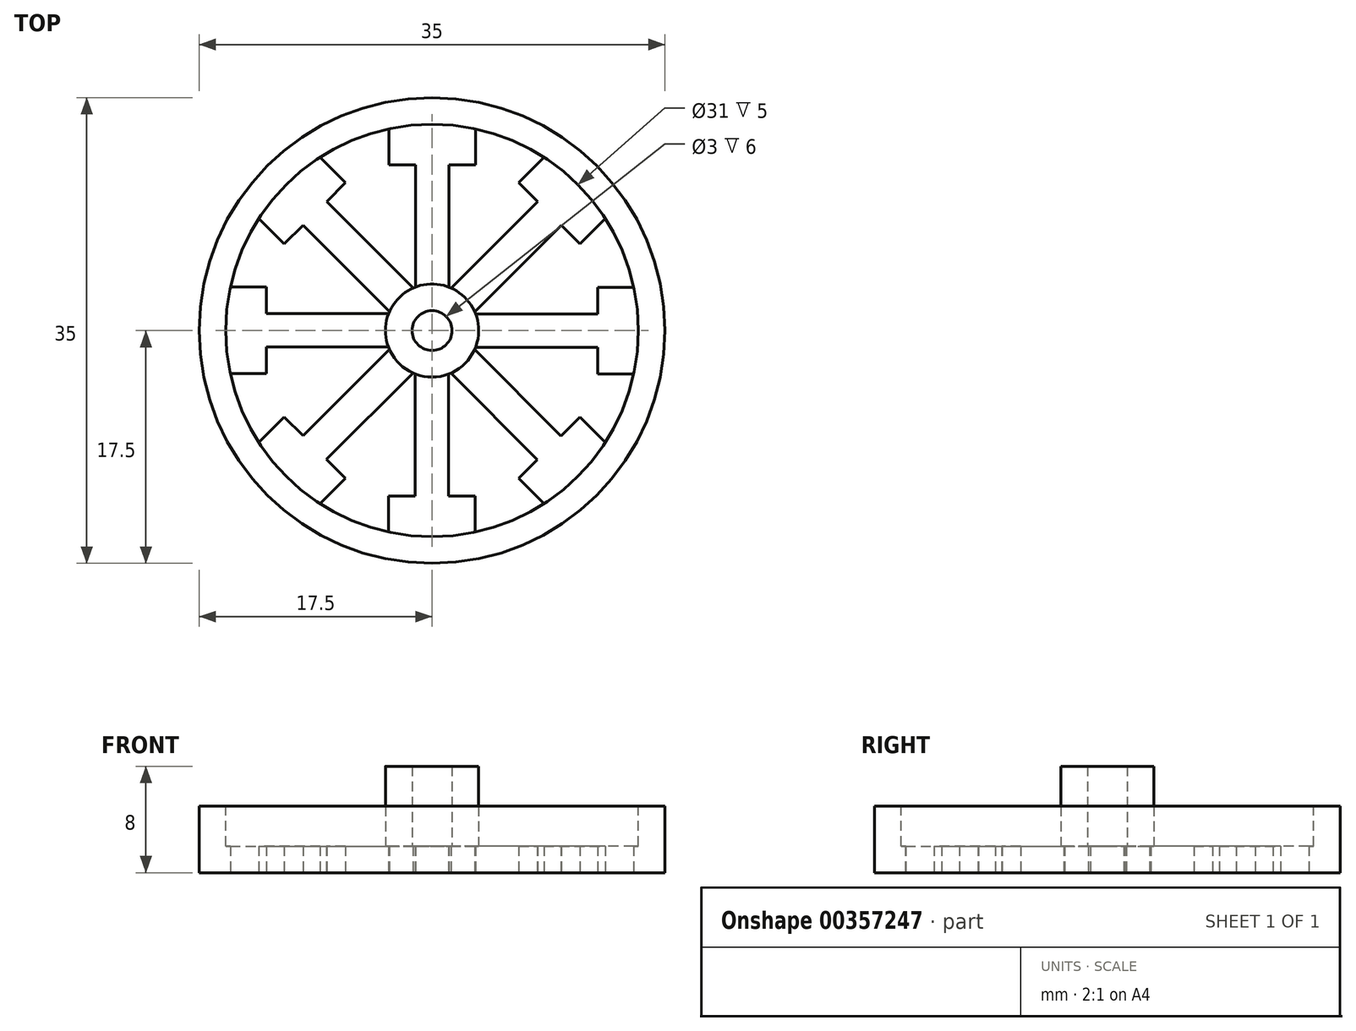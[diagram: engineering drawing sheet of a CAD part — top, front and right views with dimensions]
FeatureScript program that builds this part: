
annotation { "Feature Type Name" : "Feature", "Feature Type Description" : "" }
export const myFeature = defineFeature(function(context is Context, id is Id, definition is map)
    precondition{}
    {
        {
            var Q0;
            Q0=qCreatedBy(makeId("Top.planeOp"),FACE);
            var sketch = newSketch(context, id + "F0", { "sketchPlane" : qUnion([Q0])});
            skCircle(sketch, "E0", {"center": v(0, 0) * mm, "radius": 17.5 * mm});
            skSolve(sketch);
        }
        {
            var Q0;
            Q0=makeQuery(id+"F0.imprint","IMPRINT",FACE,{"disambiguationData":[TD([[makeQuery(id+"F0.imprint","IMPRINT",EDGE,{"derivedFrom":sQuery(id+"F0.wireOp",EDGE,"E0")}),1.0]])]});
            extrude(context, id + "F1", {"entities" : qUnion([Q0]), "depth" : 5 * mm});
        }
        {
            var Q0;
            Q0=makeQuery(id+"F1.opExtrude","CAP_FACE",FACE,{"disambiguationData":[OSD([sQuery(id+"F0.wireOp",EDGE,"E0")])],"isStart":false});
            var sketch = newSketch(context, id + "F2", { "sketchPlane" : qUnion([Q0])});
            skCircle(sketch, "E1", {"center": v(0, 0) * mm, "radius": 15.5 * mm});
            skSolve(sketch);
        }
        {
            var Q0;
            Q0=makeQuery(id+"F2.imprint","IMPRINT",FACE,{"disambiguationData":[TD([[makeQuery(id+"F2.imprint","IMPRINT",EDGE,{"derivedFrom":sQuery(id+"F2.wireOp",EDGE,"E1")}),1.0]])]});
            extrude(context, id + "F3", {"entities" : qUnion([Q0]), "operationType" : NewBodyOperationType.REMOVE, "oppositeDirection" : true, "depth" : 3 * mm});
        }
        {
            var Q0;
            Q0=makeQuery(id+"F1.opExtrude","CAP_FACE",FACE,{"disambiguationData":[OSD([sQuery(id+"F0.wireOp",EDGE,"E0")])],"isStart":true});
            var sketch = newSketch(context, id + "F4", { "sketchPlane" : qUnion([Q0])});
            skCircle(sketch, "E2", {"center": v(0, 0) * mm, "radius": 1.5 * mm});
            skCircle(sketch, "E3", {"center": v(0, 0) * mm, "radius": 3.5 * mm});
            skCircle(sketch, "E4", {"center": v(0, 0) * mm, "radius": 15.5 * mm});
            skSolve(sketch);
        }
        {
            var Q0;
            Q0=makeQuery(id+"F3.boolean.opBoolean","COPY",FACE,{"derivedFrom":makeQuery(id+"F3.opExtrude","CAP_FACE",FACE,{"disambiguationData":[OSD([sQuery(id+"F2.wireOp",EDGE,"E1")])],"isStart":false})});
            var sketch = newSketch(context, id + "F5", { "sketchPlane" : qUnion([Q0])});
            skCircle(sketch, "E5", {"center": v(0, 0) * mm, "radius": 1.5 * mm});
            skCircle(sketch, "E6", {"center": v(0, 0) * mm, "radius": 3.5 * mm});
            skSolve(sketch);
        }
        {
            var Q0;
            Q0 = qSketchRegion(id + "F5", true);
            extrude(context, id + "F6", {"entities" : qUnion([Q0]), "operationType" : NewBodyOperationType.ADD, "depth" : 6 * mm});
        }
        {
            var Q0;
            Q0=makeQuery(id+"F4.imprint","IMPRINT",FACE,{"disambiguationData":[TD([[makeQuery(id+"F4.imprint","IMPRINT",EDGE,{"derivedFrom":sQuery(id+"F4.wireOp",EDGE,"E3")}),-1.0]])]});
            var sketch = newSketch(context, id + "F7", { "sketchPlane" : qUnion([Q0])});
            skLineSegment(sketch, "E7", {"start": v(-1.26, 2.45) * mm, "end": v(-1.26, 12.45) * mm});
            skLineSegment(sketch, "E8", {"start": v(1.25, 2.45) * mm, "end": v(1.25, 12.45) * mm});
            skLineSegment(sketch, "E9", {"start": v(1.25, 12.45) * mm, "end": v(3.25, 12.45) * mm});
            skLineSegment(sketch, "E10", {"start": v(3.25, 12.45) * mm, "end": v(3.25, 15.46) * mm});
            skLineSegment(sketch, "E11", {"start": v(-1.26, 12.45) * mm, "end": v(-3.26, 12.45) * mm});
            skLineSegment(sketch, "E12", {"start": v(-3.26, 12.45) * mm, "end": v(-3.26, 15.6) * mm});
            skLineSegment(sketch, "E13.1.0", {"start": v(-2.63, 0.84) * mm, "end": v(-9.7, 7.91) * mm});
            skLineSegment(sketch, "E13.1.1", {"start": v(-0.85, 2.62) * mm, "end": v(-7.92, 9.69) * mm});
            skLineSegment(sketch, "E13.1.2", {"start": v(-7.92, 9.69) * mm, "end": v(-6.5, 11.1) * mm});
            skLineSegment(sketch, "E13.1.3", {"start": v(-6.5, 11.1) * mm, "end": v(-8.63, 13.23) * mm});
            skLineSegment(sketch, "E13.1.4", {"start": v(-11.11, 6.5) * mm, "end": v(-13.33, 8.72) * mm});
            skLineSegment(sketch, "E13.1.5", {"start": v(-9.7, 7.91) * mm, "end": v(-11.11, 6.5) * mm});
            skLineSegment(sketch, "E13.2.0", {"start": v(-2.45, -1.26) * mm, "end": v(-12.45, -1.26) * mm});
            skLineSegment(sketch, "E13.2.1", {"start": v(-2.45, 1.25) * mm, "end": v(-12.45, 1.25) * mm});
            skLineSegment(sketch, "E13.2.2", {"start": v(-12.45, 1.25) * mm, "end": v(-12.45, 3.25) * mm});
            skLineSegment(sketch, "E13.2.3", {"start": v(-12.45, 3.25) * mm, "end": v(-15.46, 3.25) * mm});
            skLineSegment(sketch, "E13.2.4", {"start": v(-12.45, -3.26) * mm, "end": v(-15.6, -3.26) * mm});
            skLineSegment(sketch, "E13.2.5", {"start": v(-12.45, -1.26) * mm, "end": v(-12.45, -3.26) * mm});
            skLineSegment(sketch, "E13.3.0", {"start": v(-0.84, -2.63) * mm, "end": v(-7.91, -9.7) * mm});
            skLineSegment(sketch, "E13.3.1", {"start": v(-2.62, -0.85) * mm, "end": v(-9.69, -7.92) * mm});
            skLineSegment(sketch, "E13.3.2", {"start": v(-9.69, -7.92) * mm, "end": v(-11.1, -6.5) * mm});
            skLineSegment(sketch, "E13.3.3", {"start": v(-11.1, -6.5) * mm, "end": v(-13.23, -8.63) * mm});
            skLineSegment(sketch, "E13.3.4", {"start": v(-6.5, -11.11) * mm, "end": v(-8.72, -13.33) * mm});
            skLineSegment(sketch, "E13.3.5", {"start": v(-7.91, -9.7) * mm, "end": v(-6.5, -11.11) * mm});
            skLineSegment(sketch, "E13.4.0", {"start": v(1.26, -2.45) * mm, "end": v(1.26, -12.45) * mm});
            skLineSegment(sketch, "E13.4.1", {"start": v(-1.25, -2.45) * mm, "end": v(-1.25, -12.45) * mm});
            skLineSegment(sketch, "E13.4.2", {"start": v(-1.25, -12.45) * mm, "end": v(-3.25, -12.45) * mm});
            skLineSegment(sketch, "E13.4.3", {"start": v(-3.25, -12.45) * mm, "end": v(-3.25, -15.46) * mm});
            skLineSegment(sketch, "E13.4.4", {"start": v(3.26, -12.45) * mm, "end": v(3.26, -15.6) * mm});
            skLineSegment(sketch, "E13.4.5", {"start": v(1.26, -12.45) * mm, "end": v(3.26, -12.45) * mm});
            skLineSegment(sketch, "E13.5.0", {"start": v(2.63, -0.84) * mm, "end": v(9.7, -7.91) * mm});
            skLineSegment(sketch, "E13.5.1", {"start": v(0.85, -2.62) * mm, "end": v(7.92, -9.69) * mm});
            skLineSegment(sketch, "E13.5.2", {"start": v(7.92, -9.69) * mm, "end": v(6.5, -11.1) * mm});
            skLineSegment(sketch, "E13.5.3", {"start": v(6.5, -11.1) * mm, "end": v(8.63, -13.23) * mm});
            skLineSegment(sketch, "E13.5.4", {"start": v(11.11, -6.5) * mm, "end": v(13.33, -8.72) * mm});
            skLineSegment(sketch, "E13.5.5", {"start": v(9.7, -7.91) * mm, "end": v(11.11, -6.5) * mm});
            skLineSegment(sketch, "E13.6.0", {"start": v(2.45, 1.26) * mm, "end": v(12.45, 1.26) * mm});
            skLineSegment(sketch, "E13.6.1", {"start": v(2.45, -1.25) * mm, "end": v(12.45, -1.25) * mm});
            skLineSegment(sketch, "E13.6.2", {"start": v(12.45, -1.25) * mm, "end": v(12.45, -3.25) * mm});
            skLineSegment(sketch, "E13.6.3", {"start": v(12.45, -3.25) * mm, "end": v(15.46, -3.25) * mm});
            skLineSegment(sketch, "E13.6.4", {"start": v(12.45, 3.26) * mm, "end": v(15.6, 3.26) * mm});
            skLineSegment(sketch, "E13.6.5", {"start": v(12.45, 1.26) * mm, "end": v(12.45, 3.26) * mm});
            skLineSegment(sketch, "E13.7.0", {"start": v(0.84, 2.63) * mm, "end": v(7.91, 9.7) * mm});
            skLineSegment(sketch, "E13.7.1", {"start": v(2.62, 0.85) * mm, "end": v(9.69, 7.92) * mm});
            skLineSegment(sketch, "E13.7.2", {"start": v(9.69, 7.92) * mm, "end": v(11.1, 6.5) * mm});
            skLineSegment(sketch, "E13.7.3", {"start": v(11.1, 6.5) * mm, "end": v(13.23, 8.63) * mm});
            skLineSegment(sketch, "E13.7.4", {"start": v(6.5, 11.11) * mm, "end": v(8.72, 13.33) * mm});
            skLineSegment(sketch, "E13.7.5", {"start": v(7.91, 9.7) * mm, "end": v(6.5, 11.11) * mm});
            skPoint(sketch, "E13.center", {"position": v(0, 0) * mm});
            skSolve(sketch);
        }
        {
            var Q0;
            {var subQ0=sQuery(id+"F7.wireOp",EDGE,"E13.3.5");Q0=makeQuery(id+"F7.imprint","IMPRINT",FACE,{"disambiguationData":[TD([[makeQuery(id+"F7.imprint","IMPRINT",EDGE,{"derivedFrom":subQ0}),1.0]])]});}
            var Q1;
            {var subQ0=sQuery(id+"F7.wireOp",EDGE,"E13.2.5");Q1=makeQuery(id+"F7.imprint","IMPRINT",FACE,{"disambiguationData":[TD([[makeQuery(id+"F7.imprint","IMPRINT",EDGE,{"derivedFrom":subQ0}),1.0]])]});}
            var Q2;
            {var subQ0=sQuery(id+"F7.wireOp",EDGE,"E13.1.5");Q2=makeQuery(id+"F7.imprint","IMPRINT",FACE,{"disambiguationData":[TD([[makeQuery(id+"F7.imprint","IMPRINT",EDGE,{"derivedFrom":subQ0}),1.0]])]});}
            var Q3;
            {var subQ1=sQuery(id+"F7.wireOp",EDGE,"E11");Q3=makeQuery(id+"F7.imprint","IMPRINT",FACE,{"disambiguationData":[TD([[makeQuery(id+"F7.imprint","IMPRINT",EDGE,{"derivedFrom":subQ1}),1.0]])]});}
            var Q4;
            {var subQ5=sQuery(id+"F7.wireOp",EDGE,"E9");Q4=makeQuery(id+"F7.imprint","IMPRINT",FACE,{"disambiguationData":[TD([[makeQuery(id+"F7.imprint","IMPRINT",EDGE,{"derivedFrom":subQ5}),-1.0]])]});}
            var Q5;
            {var subQ0=sQuery(id+"F7.wireOp",EDGE,"E13.4.5");Q5=makeQuery(id+"F7.imprint","IMPRINT",FACE,{"disambiguationData":[TD([[makeQuery(id+"F7.imprint","IMPRINT",EDGE,{"derivedFrom":subQ0}),1.0]])]});}
            var Q6;
            {var subQ0=sQuery(id+"F7.wireOp",EDGE,"E13.5.5");Q6=makeQuery(id+"F7.imprint","IMPRINT",FACE,{"disambiguationData":[TD([[makeQuery(id+"F7.imprint","IMPRINT",EDGE,{"derivedFrom":subQ0}),1.0]])]});}
            var Q7;
            {var subQ0=sQuery(id+"F7.wireOp",EDGE,"E13.6.5");Q7=makeQuery(id+"F7.imprint","IMPRINT",FACE,{"disambiguationData":[TD([[makeQuery(id+"F7.imprint","IMPRINT",EDGE,{"derivedFrom":subQ0}),1.0]])]});}
            extrude(context, id + "F8", {"entities" : qUnion([Q0, Q1, Q2, Q3, Q4, Q5, Q6, Q7]), "operationType" : NewBodyOperationType.REMOVE, "oppositeDirection" : true, "depth" : 25 * mm});
        }
    });
